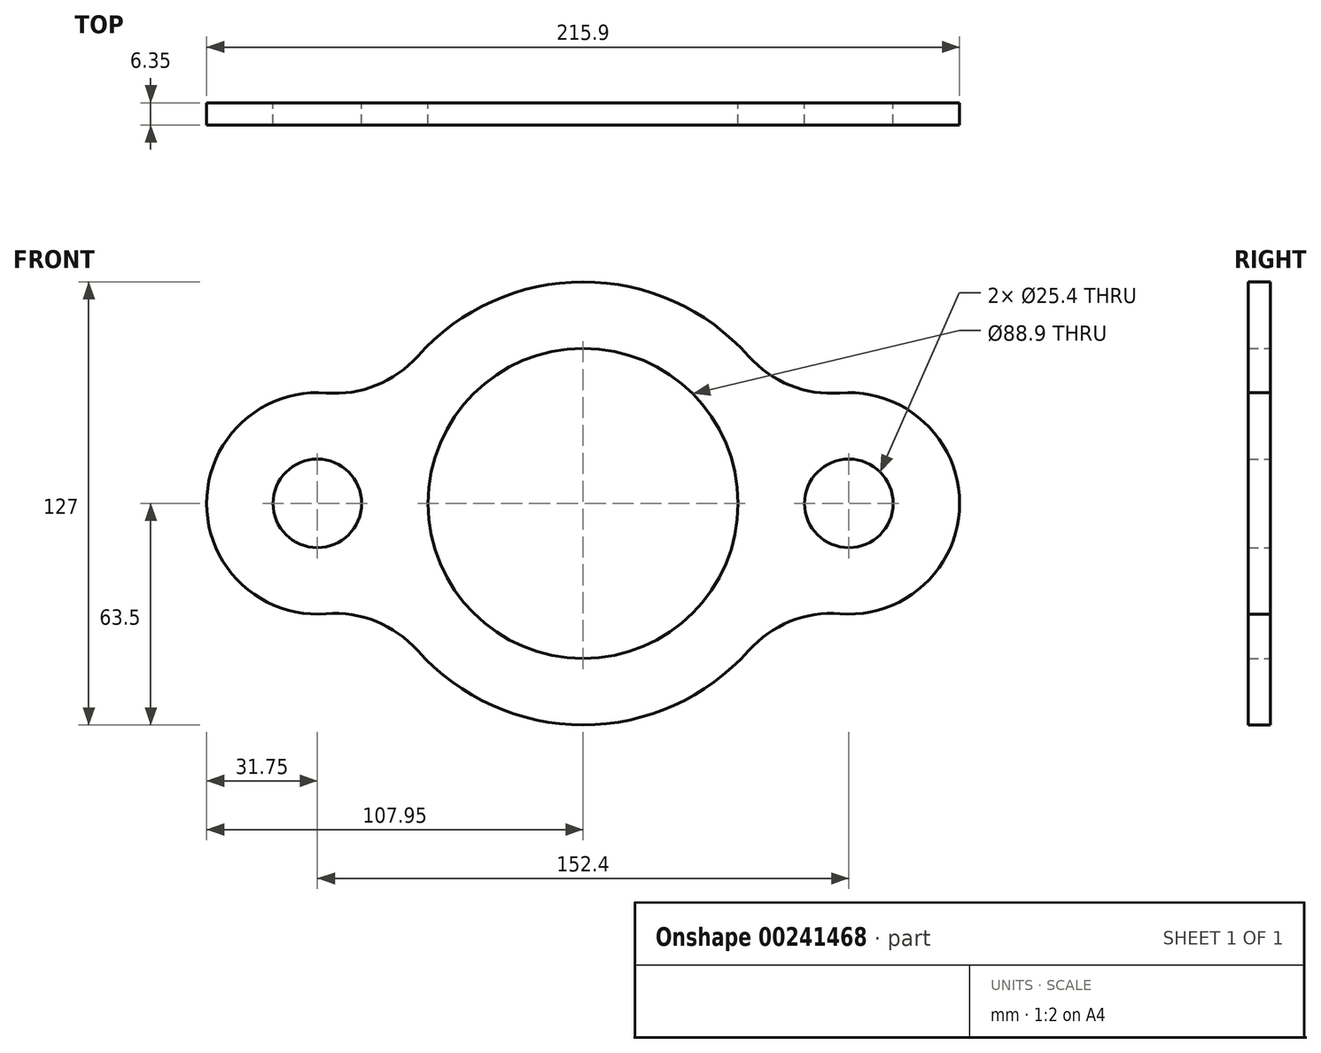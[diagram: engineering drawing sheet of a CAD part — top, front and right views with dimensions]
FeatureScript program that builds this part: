
annotation { "Feature Type Name" : "Feature", "Feature Type Description" : "" }
export const myFeature = defineFeature(function(context is Context, id is Id, definition is map)
    precondition{}
    {
        {
            var Q0;
            Q0=qCreatedBy(makeId("Front.planeOp"),FACE);
            var sketch = newSketch(context, id + "F0", { "sketchPlane" : qUnion([Q0])});
            skArc(sketch, "E0", {"start": v(-47.45, -42.2) * mm, "mid": v(0, -63.5) * mm, "end": v(47.45, -42.2) * mm});
            skCircle(sketch, "E1", {"center": v(0, 0) * mm, "radius": 44.45 * mm});
            skLineSegment(sketch, "E2", {"start": v(0, 0) * mm, "end": v(-76.2, 0) * mm, "construction": true});
            skArc(sketch, "E3", {"start": v(-73.69, 31.65) * mm, "mid": v(-107.95, 0) * mm, "end": v(-73.69, -31.65) * mm});
            skCircle(sketch, "E4", {"center": v(-76.2, 0) * mm, "radius": 12.7 * mm});
            skArc(sketch, "E5", {"start": v(73.69, -31.65) * mm, "mid": v(107.95, 0) * mm, "end": v(73.69, 31.65) * mm});
            skCircle(sketch, "E6", {"center": v(76.2, 0) * mm, "radius": 12.7 * mm});
            skPoint(sketch, "E7.visualSharp", {"position": v(-57.94, 25.98) * mm});
            skArc(sketch, "E7.filletArc", {"start": v(-73.69, 31.65) * mm, "mid": v(-59.33, 33.84) * mm, "end": v(-47.45, 42.2) * mm});
            skPoint(sketch, "E8.visualSharp", {"position": v(-57.94, -25.98) * mm});
            skArc(sketch, "E8.filletArc", {"start": v(-47.45, -42.2) * mm, "mid": v(-59.33, -33.84) * mm, "end": v(-73.69, -31.65) * mm});
            skArc(sketch, "E9.trimOffspring", {"start": v(47.45, 42.2) * mm, "mid": v(0, 63.5) * mm, "end": v(-47.45, 42.2) * mm});
            skPoint(sketch, "E10.visualSharp", {"position": v(57.94, -25.98) * mm});
            skArc(sketch, "E10.filletArc", {"start": v(73.69, -31.65) * mm, "mid": v(59.33, -33.84) * mm, "end": v(47.45, -42.2) * mm});
            skPoint(sketch, "E11.visualSharp", {"position": v(57.94, 25.98) * mm});
            skArc(sketch, "E11.filletArc", {"start": v(47.45, 42.2) * mm, "mid": v(59.33, 33.84) * mm, "end": v(73.69, 31.65) * mm});
            skLineSegment(sketch, "E12", {"start": v(0, 0) * mm, "end": v(76.2, 0) * mm, "construction": true});
            skSolve(sketch);
        }
        {
            var Q0;
            Q0 = qSketchRegion(id + "F0", true);
            extrude(context, id + "F1", {"entities" : qUnion([Q0]), "depth" : 6.35 * mm});
        }
    });
